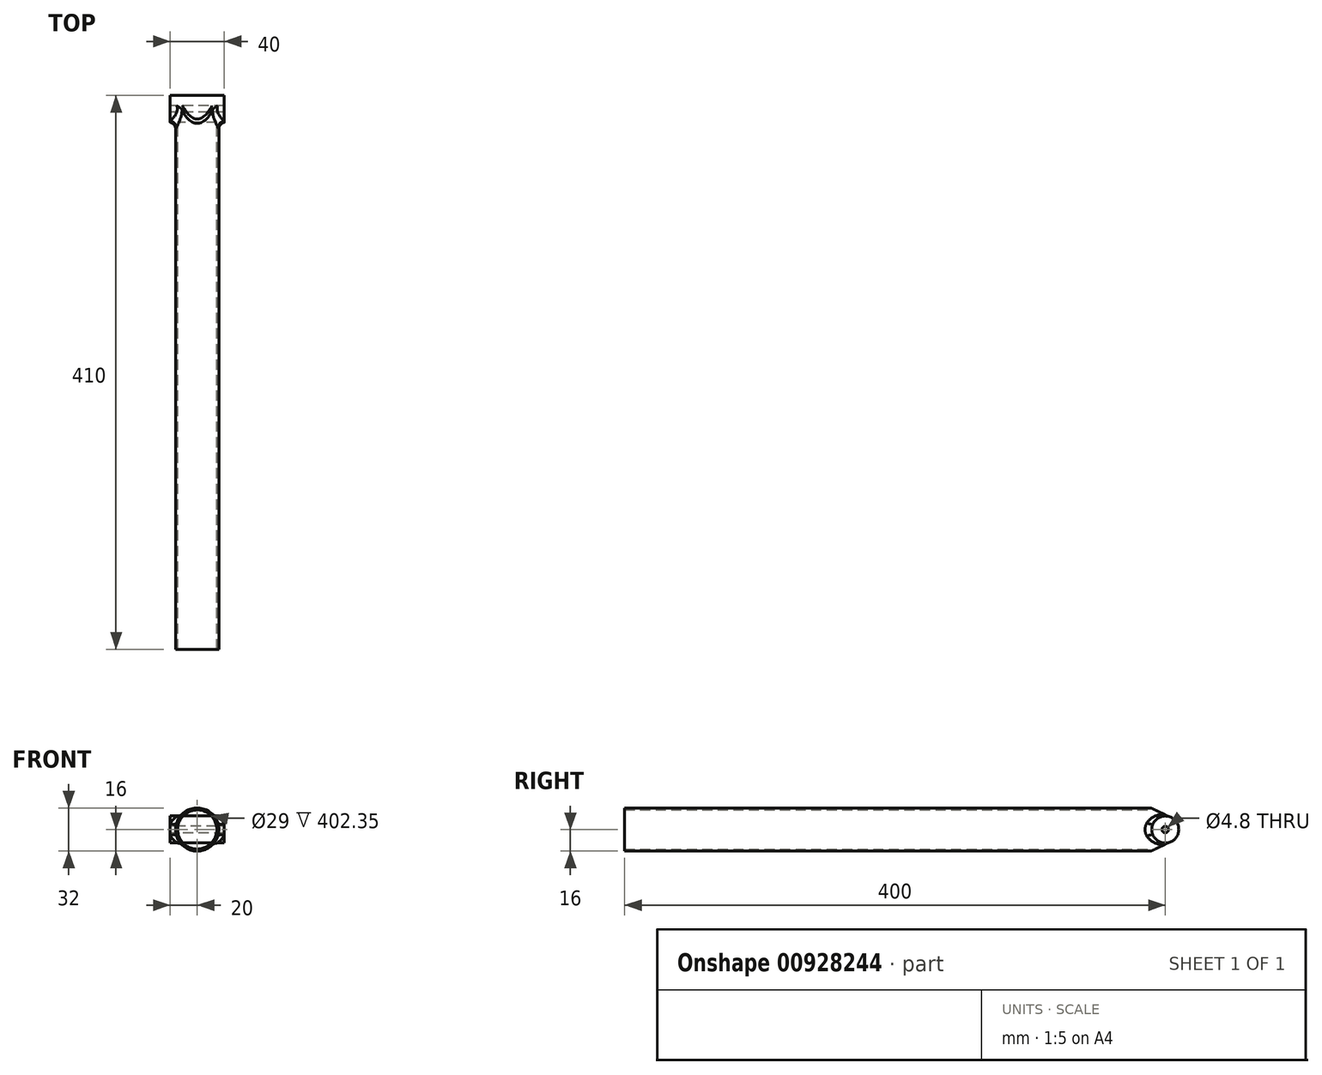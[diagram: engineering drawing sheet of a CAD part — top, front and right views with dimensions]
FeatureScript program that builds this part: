
annotation { "Feature Type Name" : "Feature", "Feature Type Description" : "" }
export const myFeature = defineFeature(function(context is Context, id is Id, definition is map)
    precondition{}
    {
        {
            var Q0;
            Q0=qCreatedBy(makeId("Right.planeOp"),FACE);
            var sketch = newSketch(context, id + "F0", { "sketchPlane" : qUnion([Q0])});
            skCircle(sketch, "E0", {"center": v(0, 0) * mm, "radius": 10 * mm});
            skSolve(sketch);
        }
        {
            var Q0;
            Q0=qCreatedBy(makeId("Front.planeOp"),FACE);
            var sketch = newSketch(context, id + "F1", { "sketchPlane" : qUnion([Q0])});
            skCircle(sketch, "E1", {"center": v(0, 0) * mm, "radius": 16 * mm});
            skCircle(sketch, "E2", {"center": v(0, 0) * mm, "radius": 14.5 * mm});
            skSolve(sketch);
        }
        {
            var Q0;
            Q0=qCreatedBy(makeId("Right.planeOp"),FACE);
            var sketch = newSketch(context, id + "F2", { "sketchPlane" : qUnion([Q0])});
            skCircle(sketch, "E3", {"center": v(0, 0) * mm, "radius": 2.4 * mm});
            skArc(sketch, "E4", {"start": v(4.23, -9.06) * mm, "mid": v(10, 0) * mm, "end": v(4.23, 9.06) * mm});
            skLineSegment(sketch, "E5", {"start": v(-22.96, 21.74) * mm, "end": v(4.23, 9.06) * mm});
            skLineSegment(sketch, "E6", {"start": v(-22.96, -21.74) * mm, "end": v(4.23, -9.06) * mm});
            skLineSegment(sketch, "E7.0", {"start": v(-19.58, -29) * mm, "end": v(7.6, -16.31) * mm});
            skArc(sketch, "E7.1", {"start": v(7.6, -16.31) * mm, "mid": v(18, 0) * mm, "end": v(7.6, 16.31) * mm});
            skLineSegment(sketch, "E7.2", {"start": v(-19.58, 29) * mm, "end": v(7.6, 16.31) * mm});
            skLineSegment(sketch, "E8", {"start": v(-22.96, 21.74) * mm, "end": v(-19.58, 29) * mm});
            skLineSegment(sketch, "E9", {"start": v(-22.96, -21.74) * mm, "end": v(-19.58, -29) * mm});
            skSolve(sketch);
        }
        {
            var Q0;
            Q0=qSketchRegion(id+"F0",true);
            extrude(context, id + "F3", {"entities" : qUnion([Q0]), "endBound" : BoundingType.SYMMETRIC, "depth" : 40 * mm, "offsetDistance" : 25 * mm});
        }
        {
            var Q0;
            Q0=qSketchRegion(id+"F1",true);
            extrude(context, id + "F4", {"entities" : qUnion([Q0]), "operationType" : NewBodyOperationType.ADD, "depth" : 400 * mm, "offsetDistance" : 25 * mm});
        }
        {
            var Q0;
            Q0=qSketchRegion(id+"F2",true);
            extrude(context, id + "F5", {"entities" : qUnion([Q0]), "operationType" : NewBodyOperationType.REMOVE, "endBound" : BoundingType.SYMMETRIC, "depth" : 50 * mm, "offsetDistance" : 25 * mm});
        }
        {
            var Q0;
            Q0=makeQuery(id+"FFgx48Y584oPXpA_1.boolean.opBoolean","INTERSECT",EDGE,{"derivedFrom":[makeQuery(id+"F3.opExtrude","SWEPT_FACE",FACE,{"disambiguationData":[OSD([sQuery(id+"F0.wireOp",EDGE,"E0")])]}),makeQuery(id+"FFgx48Y584oPXpA_1.opExtrude","CAP_FACE",FACE,{"disambiguationData":[OSD([sQuery(id+"FfMeU5U8mY6v9wT_1.wireOp",EDGE,"pgj4ZOgv-2Mio-jAAW-4sQG-o3xthrZsPGz2"),sQuery(id+"FfMeU5U8mY6v9wT_1.wireOp",EDGE,"mQYQay1I-H9bq-6uqX-I5H7-E4qIbZSJgSRT"),sQuery(id+"FfMeU5U8mY6v9wT_1.wireOp",EDGE,"DYCeb9kw-8QuW-U8y1-hKow-YMbHlAbmmqvh"),sQuery(id+"FfMeU5U8mY6v9wT_1.wireOp",EDGE,"k244k26J-vxc9-2PJk-dX7w-ivl2OcQDMpD1")])],"isStart":false})]});
            var Q1;
            Q1=makeQuery(id+"FFgx48Y584oPXpA_1.boolean.opBoolean","INTERSECT",EDGE,{"derivedFrom":[makeQuery(id+"F3.opExtrude","SWEPT_FACE",FACE,{"disambiguationData":[OSD([sQuery(id+"F0.wireOp",EDGE,"E0")])]}),makeQuery(id+"FFgx48Y584oPXpA_1.opExtrude","CAP_FACE",FACE,{"disambiguationData":[OSD([sQuery(id+"FfMeU5U8mY6v9wT_1.wireOp",EDGE,"pgj4ZOgv-2Mio-jAAW-4sQG-o3xthrZsPGz2"),sQuery(id+"FfMeU5U8mY6v9wT_1.wireOp",EDGE,"mQYQay1I-H9bq-6uqX-I5H7-E4qIbZSJgSRT"),sQuery(id+"FfMeU5U8mY6v9wT_1.wireOp",EDGE,"DYCeb9kw-8QuW-U8y1-hKow-YMbHlAbmmqvh"),sQuery(id+"FfMeU5U8mY6v9wT_1.wireOp",EDGE,"k244k26J-vxc9-2PJk-dX7w-ivl2OcQDMpD1")])],"isStart":true})]});
            var Q2;
            Q2=makeQuery(id+"FFgx48Y584oPXpA_1.boolean.opBoolean","INTERSECT",EDGE,{"derivedFrom":[makeQuery(id+"F3.opExtrude","SWEPT_FACE",FACE,{"disambiguationData":[OSD([sQuery(id+"F0.wireOp",EDGE,"E0")])]}),makeQuery(id+"FFgx48Y584oPXpA_1.opExtrude","CAP_FACE",FACE,{"disambiguationData":[OSD([sQuery(id+"FfMeU5U8mY6v9wT_1.wireOp",EDGE,"dc815bda-6277-4e12-9dc5-4a5bf60224480.MirrorCS"),sQuery(id+"FfMeU5U8mY6v9wT_1.wireOp",EDGE,"bc4b4c24-1870-4b8e-973b-4f0e4dad02bf0.MirrorCS"),sQuery(id+"FfMeU5U8mY6v9wT_1.wireOp",EDGE,"e8936b14-8fb7-475c-977b-ec83b2eaadce0.MirrorCS"),sQuery(id+"FfMeU5U8mY6v9wT_1.wireOp",EDGE,"529e6e5d-6be8-4b6e-93d6-b0b70f2cffd30.MirrorCS")])],"isStart":false})]});
            var Q3;
            Q3=makeQuery(id+"FFgx48Y584oPXpA_1.boolean.opBoolean","INTERSECT",EDGE,{"derivedFrom":[makeQuery(id+"F3.opExtrude","SWEPT_FACE",FACE,{"disambiguationData":[OSD([sQuery(id+"F0.wireOp",EDGE,"E0")])]}),makeQuery(id+"FFgx48Y584oPXpA_1.opExtrude","CAP_FACE",FACE,{"disambiguationData":[OSD([sQuery(id+"FfMeU5U8mY6v9wT_1.wireOp",EDGE,"dc815bda-6277-4e12-9dc5-4a5bf60224480.MirrorCS"),sQuery(id+"FfMeU5U8mY6v9wT_1.wireOp",EDGE,"bc4b4c24-1870-4b8e-973b-4f0e4dad02bf0.MirrorCS"),sQuery(id+"FfMeU5U8mY6v9wT_1.wireOp",EDGE,"e8936b14-8fb7-475c-977b-ec83b2eaadce0.MirrorCS"),sQuery(id+"FfMeU5U8mY6v9wT_1.wireOp",EDGE,"529e6e5d-6be8-4b6e-93d6-b0b70f2cffd30.MirrorCS")])],"isStart":true})]});
            var Q4;
            {var subQ0=makeQuery(id+"F3.opExtrude","SWEPT_FACE",FACE,{"disambiguationData":[OSD([sQuery(id+"F0.wireOp",EDGE,"E0")])]});var subQ1=sQuery(id+"F1.wireOp",EDGE,"E1");var subQ2=makeQuery(id+"F4.opExtrude","SWEPT_FACE",FACE,{"disambiguationData":[OSD([subQ1])]});Q4=makeQuery(id+"FFgx48Y584oPXpA_1.boolean.opBoolean","SPLIT",EDGE,{"disambiguationData":[TD([makeQuery(id+"FFgx48Y584oPXpA_1.opExtrude","CAP_FACE",FACE,{"disambiguationData":[OSD([sQuery(id+"FfMeU5U8mY6v9wT_1.wireOp",EDGE,"dc815bda-6277-4e12-9dc5-4a5bf60224480.MirrorCS"),sQuery(id+"FfMeU5U8mY6v9wT_1.wireOp",EDGE,"bc4b4c24-1870-4b8e-973b-4f0e4dad02bf0.MirrorCS"),sQuery(id+"FfMeU5U8mY6v9wT_1.wireOp",EDGE,"e8936b14-8fb7-475c-977b-ec83b2eaadce0.MirrorCS"),sQuery(id+"FfMeU5U8mY6v9wT_1.wireOp",EDGE,"529e6e5d-6be8-4b6e-93d6-b0b70f2cffd30.MirrorCS")])],"isStart":true})])],"derivedFrom":makeQuery(id+"F4.boolean.opBoolean","INTERSECT",EDGE,{"disambiguationData":[OD(1.0)],"derivedFrom":[subQ0,subQ2]})});}
            var Q5;
            {var subQ0=makeQuery(id+"F3.opExtrude","SWEPT_FACE",FACE,{"disambiguationData":[OSD([sQuery(id+"F0.wireOp",EDGE,"E0")])]});var subQ1=sQuery(id+"F1.wireOp",EDGE,"E1");var subQ2=makeQuery(id+"F4.opExtrude","SWEPT_FACE",FACE,{"disambiguationData":[OSD([subQ1])]});Q5=makeQuery(id+"FFgx48Y584oPXpA_1.boolean.opBoolean","SPLIT",EDGE,{"disambiguationData":[TD([makeQuery(id+"FFgx48Y584oPXpA_1.opExtrude","CAP_FACE",FACE,{"disambiguationData":[OSD([sQuery(id+"FfMeU5U8mY6v9wT_1.wireOp",EDGE,"pgj4ZOgv-2Mio-jAAW-4sQG-o3xthrZsPGz2"),sQuery(id+"FfMeU5U8mY6v9wT_1.wireOp",EDGE,"mQYQay1I-H9bq-6uqX-I5H7-E4qIbZSJgSRT"),sQuery(id+"FfMeU5U8mY6v9wT_1.wireOp",EDGE,"DYCeb9kw-8QuW-U8y1-hKow-YMbHlAbmmqvh"),sQuery(id+"FfMeU5U8mY6v9wT_1.wireOp",EDGE,"k244k26J-vxc9-2PJk-dX7w-ivl2OcQDMpD1")])],"isStart":true})])],"derivedFrom":makeQuery(id+"F4.boolean.opBoolean","INTERSECT",EDGE,{"disambiguationData":[OD(0.0)],"derivedFrom":[subQ0,subQ2]})});}
            var Q6;
            {var subQ0=makeQuery(id+"F3.opExtrude","SWEPT_FACE",FACE,{"disambiguationData":[OSD([sQuery(id+"F0.wireOp",EDGE,"E0")])]});var subQ1=sQuery(id+"F1.wireOp",EDGE,"E1");var subQ2=makeQuery(id+"F4.opExtrude","SWEPT_FACE",FACE,{"disambiguationData":[OSD([subQ1])]});Q6=makeQuery(id+"FFgx48Y584oPXpA_1.boolean.opBoolean","SPLIT",EDGE,{"disambiguationData":[TD([makeQuery(id+"FFgx48Y584oPXpA_1.opExtrude","CAP_FACE",FACE,{"disambiguationData":[OSD([sQuery(id+"FfMeU5U8mY6v9wT_1.wireOp",EDGE,"pgj4ZOgv-2Mio-jAAW-4sQG-o3xthrZsPGz2"),sQuery(id+"FfMeU5U8mY6v9wT_1.wireOp",EDGE,"mQYQay1I-H9bq-6uqX-I5H7-E4qIbZSJgSRT"),sQuery(id+"FfMeU5U8mY6v9wT_1.wireOp",EDGE,"DYCeb9kw-8QuW-U8y1-hKow-YMbHlAbmmqvh"),sQuery(id+"FfMeU5U8mY6v9wT_1.wireOp",EDGE,"k244k26J-vxc9-2PJk-dX7w-ivl2OcQDMpD1")])],"isStart":false})])],"derivedFrom":makeQuery(id+"F4.boolean.opBoolean","INTERSECT",EDGE,{"disambiguationData":[OD(0.0)],"derivedFrom":[subQ0,subQ2]})});}
            var Q7;
            Q7=makeQuery(id+"F4.boolean.opBoolean","INTERSECT",EDGE,{"disambiguationData":[OD(1.0)],"derivedFrom":[makeQuery(id+"F3.opExtrude","SWEPT_FACE",FACE,{"disambiguationData":[OSD([sQuery(id+"F0.wireOp",EDGE,"E0")])]}),makeQuery(id+"F4.opExtrude","CAP_FACE",FACE,{"disambiguationData":[OSD([sQuery(id+"F1.wireOp",EDGE,"E1"),sQuery(id+"F1.wireOp",EDGE,"E2")])],"isStart":true})]});
            var Q8;
            Q8=makeQuery(id+"F4.boolean.opBoolean","INTERSECT",EDGE,{"disambiguationData":[OD(3.0)],"derivedFrom":[makeQuery(id+"F3.opExtrude","SWEPT_FACE",FACE,{"disambiguationData":[OSD([sQuery(id+"F0.wireOp",EDGE,"E0")])]}),makeQuery(id+"F4.opExtrude","CAP_FACE",FACE,{"disambiguationData":[OSD([sQuery(id+"F1.wireOp",EDGE,"E1"),sQuery(id+"F1.wireOp",EDGE,"E2")])],"isStart":true})]});
            var Q9;
            Q9=makeQuery(id+"F4.boolean.opBoolean","INTERSECT",EDGE,{"disambiguationData":[OD(2.0)],"derivedFrom":[makeQuery(id+"F3.opExtrude","SWEPT_FACE",FACE,{"disambiguationData":[OSD([sQuery(id+"F0.wireOp",EDGE,"E0")])]}),makeQuery(id+"F4.opExtrude","CAP_FACE",FACE,{"disambiguationData":[OSD([sQuery(id+"F1.wireOp",EDGE,"E1"),sQuery(id+"F1.wireOp",EDGE,"E2")])],"isStart":true})]});
            var Q10;
            Q10=makeQuery(id+"F4.boolean.opBoolean","INTERSECT",EDGE,{"disambiguationData":[OD(0.0)],"derivedFrom":[makeQuery(id+"F3.opExtrude","SWEPT_FACE",FACE,{"disambiguationData":[OSD([sQuery(id+"F0.wireOp",EDGE,"E0")])]}),makeQuery(id+"F4.opExtrude","CAP_FACE",FACE,{"disambiguationData":[OSD([sQuery(id+"F1.wireOp",EDGE,"E1"),sQuery(id+"F1.wireOp",EDGE,"E2")])],"isStart":true})]});
            var Q11;
            {var subQ0=makeQuery(id+"F3.opExtrude","SWEPT_FACE",FACE,{"disambiguationData":[OSD([sQuery(id+"F0.wireOp",EDGE,"E0")])]});var subQ1=sQuery(id+"F1.wireOp",EDGE,"E1");var subQ2=makeQuery(id+"F4.opExtrude","SWEPT_FACE",FACE,{"disambiguationData":[OSD([subQ1])]});Q11=makeQuery(id+"FFgx48Y584oPXpA_1.boolean.opBoolean","SPLIT",EDGE,{"disambiguationData":[TD([makeQuery(id+"FFgx48Y584oPXpA_1.opExtrude","CAP_FACE",FACE,{"disambiguationData":[OSD([sQuery(id+"FfMeU5U8mY6v9wT_1.wireOp",EDGE,"dc815bda-6277-4e12-9dc5-4a5bf60224480.MirrorCS"),sQuery(id+"FfMeU5U8mY6v9wT_1.wireOp",EDGE,"bc4b4c24-1870-4b8e-973b-4f0e4dad02bf0.MirrorCS"),sQuery(id+"FfMeU5U8mY6v9wT_1.wireOp",EDGE,"e8936b14-8fb7-475c-977b-ec83b2eaadce0.MirrorCS"),sQuery(id+"FfMeU5U8mY6v9wT_1.wireOp",EDGE,"529e6e5d-6be8-4b6e-93d6-b0b70f2cffd30.MirrorCS")])],"isStart":false})])],"derivedFrom":makeQuery(id+"F4.boolean.opBoolean","INTERSECT",EDGE,{"disambiguationData":[OD(1.0)],"derivedFrom":[subQ0,subQ2]})});}
            fillet(context, id + "F6", {"entities" : qUnion([Q0, Q1, Q2, Q3, Q4, Q5, Q6, Q7, Q8, Q9, Q10, Q11]), "radius" : 5 * mm, "tangentPropagation" : true});
        }
    });
